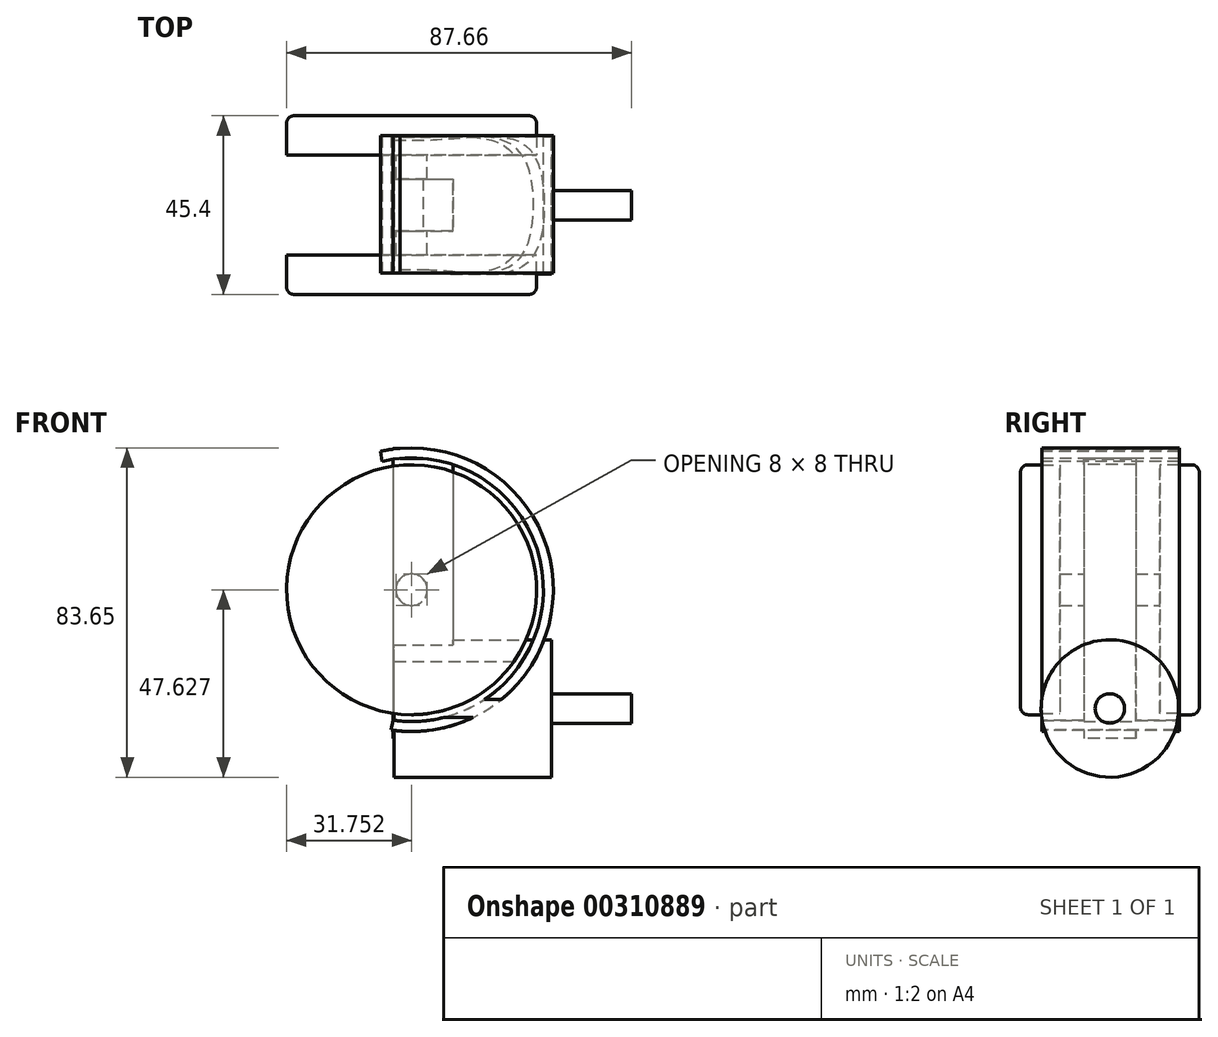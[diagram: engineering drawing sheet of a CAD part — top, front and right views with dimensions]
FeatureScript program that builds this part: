
annotation { "Feature Type Name" : "Feature", "Feature Type Description" : "" }
export const myFeature = defineFeature(function(context is Context, id is Id, definition is map)
    precondition{}
    {
        {
            var Q0;
            Q0=qCreatedBy(makeId("Front.planeOp"),FACE);
            var sketch = newSketch(context, id + "F0", { "sketchPlane" : qUnion([Q0])});
            skCircle(sketch, "E0", {"center": v(-55.9, 37.76) * mm, "radius": 4 * mm});
            skSolve(sketch);
        }
        {
            var Q0;
            Q0 = qSketchRegion(id + "F0", true);
            extrude(context, id + "F1", {"entities" : qUnion([Q0]), "depth" : 12.7 * mm});
        }
        {
            var Q0;
            Q0=makeQuery(id+"F1.opExtrude","CAP_FACE",FACE,{"disambiguationData":[OSD([sQuery(id+"F0.wireOp",EDGE,"E0")])],"isStart":false});
            var sketch = newSketch(context, id + "F2", { "sketchPlane" : qUnion([Q0])});
            skCircle(sketch, "E1", {"center": v(-55.9, 37.76) * mm, "radius": 31.75 * mm});
            skSolve(sketch);
        }
        {
            var Q0;
            Q0 = qSketchRegion(id + "F2", true);
            extrude(context, id + "F3", {"entities" : qUnion([Q0]), "operationType" : NewBodyOperationType.ADD, "depth" : 10 * mm});
        }
        {
            var Q0;
            Q0=makeQuery(id+"F3.opExtrude","CAP_EDGE",EDGE,{"disambiguationData":[OSD([sQuery(id+"F2.wireOp",EDGE,"E1")])],"isStart":false});
            fillet(context, id + "F4", {"entities" : qUnion([Q0]), "radius" : 1.9 * mm, "tangentPropagation" : true, "allowEdgeOverflow" : false});
        }
        {
            var Q0;
            Q0=makeQuery(id+"F1.opExtrude","SWEPT_BODY",BODY,{"disambiguationData":[OSD([sQuery(id+"F0.wireOp",EDGE,"E0")])]});
            var Q1;
            Q1=qCreatedBy(makeId("Front.planeOp"),FACE);
            mirror(context, id + "F5", {"operationType" : NewBodyOperationType.ADD, "entities" : qUnion([Q0]), "mirrorPlane" : qUnion([Q1])});
        }
        {
            var Q0;
            Q0=qCreatedBy(makeId("Top.planeOp"),FACE);
            var sketch = newSketch(context, id + "F6", { "sketchPlane" : qUnion([Q0])});
            skLineSegment(sketch, "E2.bottom", {"start": v(-60.65, 0) * mm, "end": v(-45.41, 0) * mm});
            skLineSegment(sketch, "E2.top", {"start": v(-60.65, 6.63) * mm, "end": v(-45.41, 6.63) * mm});
            skLineSegment(sketch, "E2.left", {"start": v(-60.65, 0) * mm, "end": v(-60.65, 6.63) * mm});
            skLineSegment(sketch, "E2.right", {"start": v(-45.41, 0) * mm, "end": v(-45.41, 6.63) * mm});
            skSolve(sketch);
        }
        {
            var Q0;
            Q0 = qSketchRegion(id + "F6", true);
            extrude(context, id + "F7", {"entities" : qUnion([Q0]), "operationType" : NewBodyOperationType.ADD, "depth" : 71.12 * mm});
        }
        {
            var Q0;
            Q0=makeQuery(id+"F1.opExtrude","SWEPT_BODY",BODY,{"disambiguationData":[OSD([sQuery(id+"F0.wireOp",EDGE,"E0")])]});
            var Q1;
            Q1=qCreatedBy(makeId("Front.planeOp"),FACE);
            mirror(context, id + "F8", {"operationType" : NewBodyOperationType.ADD, "entities" : qUnion([Q0]), "mirrorPlane" : qUnion([Q1])});
        }
        {
            var Q0;
            {var subQ0=makeQuery(id+"F7.opExtrude","CAP_FACE",FACE,{"disambiguationData":[OSD([sQuery(id+"F6.wireOp",EDGE,"E2.bottom"),sQuery(id+"F6.wireOp",EDGE,"E2.top"),sQuery(id+"F6.wireOp",EDGE,"E2.left"),sQuery(id+"F6.wireOp",EDGE,"E2.right")])],"isStart":false});Q0=makeQuery(id+"F8.boolean.opBoolean","MERGE",FACE,{"derivedFrom":[subQ0,makeQuery(id+"F8.opPattern","COPY",FACE,{"derivedFrom":subQ0,"instanceName":"1"})]});}
            var sketch = newSketch(context, id + "F9", { "sketchPlane" : qUnion([Q0])});
            skLineSegment(sketch, "E3.bottom", {"start": v(-60.65, 17.67) * mm, "end": v(-58.8, 17.67) * mm});
            skLineSegment(sketch, "E3.top", {"start": v(-60.65, -17.31) * mm, "end": v(-58.8, -17.31) * mm});
            skLineSegment(sketch, "E3.left", {"start": v(-60.65, 17.67) * mm, "end": v(-60.65, -17.31) * mm});
            skLineSegment(sketch, "E3.right", {"start": v(-58.8, 17.67) * mm, "end": v(-58.8, -17.31) * mm});
            skSolve(sketch);
        }
        {
            var Q0;
            Q0 = qSketchRegion(id + "F9", true);
            extrude(context, id + "F10", {"entities" : qUnion([Q0]), "operationType" : NewBodyOperationType.ADD, "depth" : 2.54 * mm});
        }
        {
            var Q0;
            Q0=makeQuery(id+"F10.opExtrude","SWEPT_FACE",FACE,{"disambiguationData":[OSD([sQuery(id+"F9.wireOp",EDGE,"E3.right")])]});
            var Q1;
            {var subQ0=sQuery(id+"F2.wireOp",EDGE,"E1");Q1=makeQuery(id+"F4.opFillet","BLEND_EDGE",EDGE,{"blendedFrom":[makeQuery(id+"F3.opExtrude","CAP_EDGE",EDGE,{"disambiguationData":[OSD([subQ0])],"isStart":false}),makeQuery(id+"F3.opExtrude","CAP_FACE",FACE,{"disambiguationData":[OSD([subQ0])],"isStart":false})],"blendedInto":[makeQuery(id+"F3.opExtrude","CAP_FACE",FACE,{"disambiguationData":[OSD([subQ0])],"isStart":false})]});}
            revolve(context, id + "F11", {"operationType" : NewBodyOperationType.ADD, "entities" : qUnion([Q0]), "axis" : qUnion([Q1]), "revolveType" : RevolveType.ONE_DIRECTION, "angle" : 8 * degree});
        }
        {
            var Q0;
            Q0=makeQuery(id+"F10.opExtrude","SWEPT_FACE",FACE,{"disambiguationData":[OSD([sQuery(id+"F9.wireOp",EDGE,"E3.right")])]});
            var Q1;
            {var subQ0=sQuery(id+"F2.wireOp",EDGE,"E1");Q1=makeQuery(id+"F4.opFillet","BLEND_EDGE",EDGE,{"blendedFrom":[makeQuery(id+"F3.opExtrude","CAP_EDGE",EDGE,{"disambiguationData":[OSD([subQ0])],"isStart":false}),makeQuery(id+"F3.opExtrude","CAP_FACE",FACE,{"disambiguationData":[OSD([subQ0])],"isStart":false})],"blendedInto":[makeQuery(id+"F3.opExtrude","CAP_FACE",FACE,{"disambiguationData":[OSD([subQ0])],"isStart":false})]});}
            revolve(context, id + "F12", {"operationType" : NewBodyOperationType.ADD, "entities" : qUnion([Q0]), "axis" : qUnion([Q1]), "revolveType" : RevolveType.ONE_DIRECTION, "oppositeDirection" : true, "angle" : 193 * degree});
        }
        {
            var Q0;
            Q0=qCreatedBy(makeId("Right.planeOp"),FACE);
            var sketch = newSketch(context, id + "F13", { "sketchPlane" : qUnion([Q0])});
            skCircle(sketch, "E4", {"center": v(0, 7.6) * mm, "radius": 3.75 * mm});
            skSolve(sketch);
        }
        {
            var Q0;
            Q0=makeQuery(id+"F13.imprint","IMPRINT",FACE,{"disambiguationData":[TD([[makeQuery(id+"F13.imprint","IMPRINT",EDGE,{"derivedFrom":sQuery(id+"F13.wireOp",EDGE,"E4")}),1.0]])]});
            var Q1;
            Q1=makeQuery(id+"F1.opExtrude","SWEPT_BODY",BODY,{"disambiguationData":[OSD([sQuery(id+"F0.wireOp",EDGE,"E0")])]});
            var Q2;
            Q2=makeQuery(id+"F1.opExtrude","SWEPT_BODY",BODY,{"disambiguationData":[OSD([sQuery(id+"F0.wireOp",EDGE,"E0")])]});
            extrude(context, id + "F14", {"entities" : qUnion([Q0]), "operationType" : NewBodyOperationType.ADD, "oppositeDirection" : true, "endBoundEntityBody" : qUnion([Q1]), "depth" : 20.32 * mm});
        }
        {
            var Q0;
            Q0=makeQuery(id+"F14.opExtrude","CAP_FACE",FACE,{"disambiguationData":[OSD([sQuery(id+"F13.wireOp",EDGE,"E4")])],"isStart":false});
            var sketch = newSketch(context, id + "F15", { "sketchPlane" : qUnion([Q0])});
            skCircle(sketch, "E5", {"center": v(0, 7.6) * mm, "radius": 17.46 * mm});
            skSolve(sketch);
        }
        {
            var Q0;
            Q0 = qSketchRegion(id + "F15", true);
            extrude(context, id + "F16", {"entities" : qUnion([Q0]), "operationType" : NewBodyOperationType.ADD, "depth" : 40 * mm});
        }
    });
